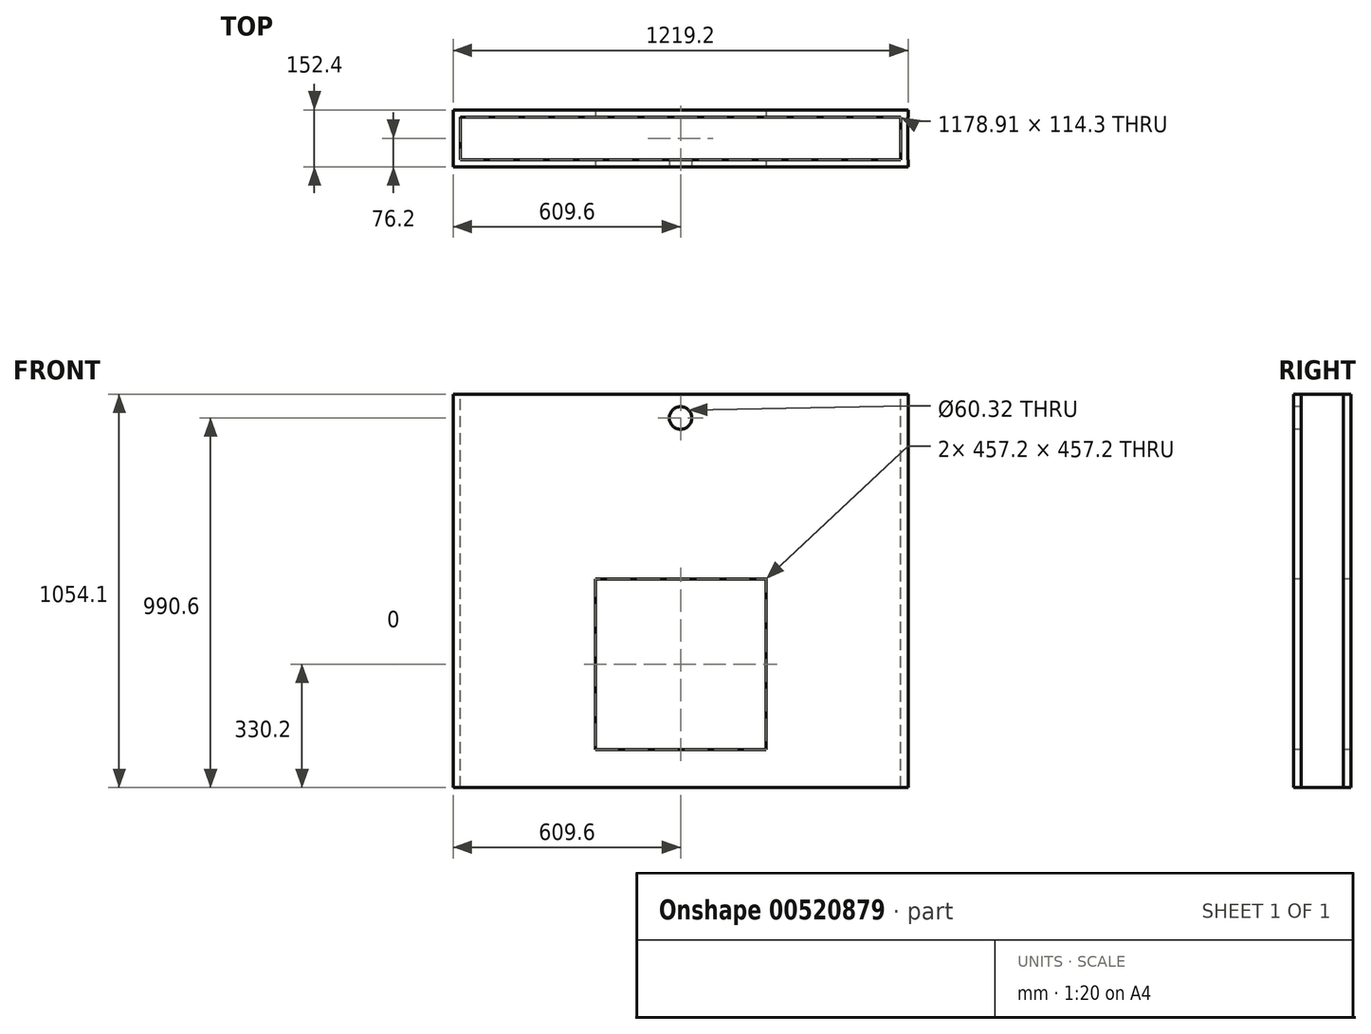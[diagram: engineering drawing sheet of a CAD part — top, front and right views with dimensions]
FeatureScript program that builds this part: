
annotation { "Feature Type Name" : "Feature", "Feature Type Description" : "" }
export const myFeature = defineFeature(function(context is Context, id is Id, definition is map)
    precondition{}
    {
        {
            var Q0;
            Q0=qCreatedBy(makeId("Top.planeOp"),FACE);
            var sketch = newSketch(context, id + "F0", { "sketchPlane" : qUnion([Q0])});
            skLineSegment(sketch, "E0.bottom", {"start": v(609.6, 76.2) * mm, "end": v(-609.6, 76.2) * mm});
            skLineSegment(sketch, "E0.top", {"start": v(609.6, -76.2) * mm, "end": v(-609.6, -76.2) * mm});
            skLineSegment(sketch, "E0.left", {"start": v(609.6, 76.2) * mm, "end": v(609.6, -76.2) * mm});
            skLineSegment(sketch, "E0.right", {"start": v(-609.6, 76.2) * mm, "end": v(-609.6, -76.2) * mm});
            skPoint(sketch, "E0.middle", {"position": v(0, 0) * mm});
            skLineSegment(sketch, "E1.bottom", {"start": v(-608.84, 57.15) * mm, "end": v(-610.36, 57.15) * mm});
            skLineSegment(sketch, "E1.top", {"start": v(-608.84, -57.15) * mm, "end": v(-610.36, -57.15) * mm});
            skLineSegment(sketch, "E1.left", {"start": v(-608.84, 57.15) * mm, "end": v(-608.84, -57.15) * mm});
            skLineSegment(sketch, "E1.right", {"start": v(-610.36, 57.15) * mm, "end": v(-610.36, -57.15) * mm});
            skPoint(sketch, "E1.middle", {"position": v(-609.6, 0) * mm});
            skLineSegment(sketch, "E2.bottom", {"start": v(610.36, 57.15) * mm, "end": v(608.84, 57.15) * mm});
            skLineSegment(sketch, "E2.top", {"start": v(610.36, -57.15) * mm, "end": v(608.84, -57.15) * mm});
            skLineSegment(sketch, "E2.left", {"start": v(610.36, 57.15) * mm, "end": v(610.36, -57.15) * mm});
            skLineSegment(sketch, "E2.right", {"start": v(608.84, 57.15) * mm, "end": v(608.84, -57.15) * mm});
            skPoint(sketch, "E2.middle", {"position": v(609.6, 0) * mm});
            skSolve(sketch);
        }
        {
            var Q0;
            {var subQ7=sQuery(id+"F0.wireOp",EDGE,"E0.bottom");Q0=makeQuery(id+"F0.imprint","IMPRINT",FACE,{"disambiguationData":[TD([[makeQuery(id+"F0.imprint","IMPRINT",EDGE,{"derivedFrom":subQ7}),1.0]])]});}
            extrude(context, id + "F1", {"entities" : qUnion([Q0]), "depth" : 1054.1 * mm, "offsetDistance" : 25.4 * mm});
        }
        {
            var Q0;
            Q0=makeQuery(id+"F1.opExtrude","SWEPT_FACE",FACE,{"disambiguationData":[OSD([sQuery(id+"F0.wireOp",EDGE,"E0.top")])]});
            var sketch = newSketch(context, id + "F2", { "sketchPlane" : qUnion([Q0])});
            skLineSegment(sketch, "E3", {"start": v(0, 0) * mm, "end": v(0, 101.6) * mm});
            skLineSegment(sketch, "E4", {"start": v(0, 101.6) * mm, "end": v(0, 330.2) * mm});
            skPoint(sketch, "E4.endSnap0", {"position": v(0, 50.8) * mm});
            skLineSegment(sketch, "E5.bottom", {"start": v(228.6, 101.6) * mm, "end": v(-228.6, 101.6) * mm});
            skLineSegment(sketch, "E5.top", {"start": v(228.6, 558.8) * mm, "end": v(-228.6, 558.8) * mm});
            skLineSegment(sketch, "E5.left", {"start": v(228.6, 101.6) * mm, "end": v(228.6, 558.8) * mm});
            skLineSegment(sketch, "E5.right", {"start": v(-228.6, 101.6) * mm, "end": v(-228.6, 558.8) * mm});
            skPoint(sketch, "E5.middle", {"position": v(0, 330.2) * mm});
            skSolve(sketch);
        }
        {
            var Q0;
            Q0=makeQuery(id+"F2.imprint","IMPRINT",FACE,{"disambiguationData":[TD([[makeQuery(id+"F2.imprint","IMPRINT",EDGE,{"derivedFrom":sQuery(id+"F2.wireOp",EDGE,"E5.top")}),1.0]])]});
            extrude(context, id + "F3", {"entities" : qUnion([Q0]), "operationType" : NewBodyOperationType.REMOVE, "oppositeDirection" : true, "depth" : 152.4 * mm, "offsetDistance" : 25.4 * mm});
        }
        {
            var Q0;
            Q0=makeQuery(id+"F1.opExtrude","CAP_FACE",FACE,{"disambiguationData":[OSD([sQuery(id+"F0.wireOp",EDGE,"E0.bottom"),sQuery(id+"F0.wireOp",EDGE,"E0.top"),sQuery(id+"F0.wireOp",EDGE,"E0.left"),sQuery(id+"F0.wireOp",EDGE,"E0.right"),sQuery(id+"F0.wireOp",EDGE,"E1.bottom"),sQuery(id+"F0.wireOp",EDGE,"E1.top"),sQuery(id+"F0.wireOp",EDGE,"E1.left"),sQuery(id+"F0.wireOp",EDGE,"E2.bottom"),sQuery(id+"F0.wireOp",EDGE,"E2.top"),sQuery(id+"F0.wireOp",EDGE,"E2.right")])],"isStart":false});
            var sketch = newSketch(context, id + "F4", { "sketchPlane" : qUnion([Q0])});
            skLineSegment(sketch, "E6.bottom", {"start": v(589.45, 57.15) * mm, "end": v(-589.45, 57.15) * mm});
            skLineSegment(sketch, "E6.top", {"start": v(589.45, -57.15) * mm, "end": v(-589.45, -57.15) * mm});
            skLineSegment(sketch, "E6.left", {"start": v(589.45, 57.15) * mm, "end": v(589.45, -57.15) * mm});
            skLineSegment(sketch, "E6.right", {"start": v(-589.45, 57.15) * mm, "end": v(-589.45, -57.15) * mm});
            skPoint(sketch, "E6.middle", {"position": v(0, 0) * mm});
            skSolve(sketch);
        }
        {
            var Q0;
            Q0=makeQuery(id+"F4.imprint","IMPRINT",FACE,{"disambiguationData":[TD([[makeQuery(id+"F4.imprint","IMPRINT",EDGE,{"derivedFrom":sQuery(id+"F4.wireOp",EDGE,"E6.bottom")}),1.0]])]});
            extrude(context, id + "F5", {"entities" : qUnion([Q0]), "operationType" : NewBodyOperationType.REMOVE, "oppositeDirection" : true, "depth" : 1270 * mm, "offsetDistance" : 25.4 * mm});
        }
        {
            var Q0;
            Q0=makeQuery(id+"F1.opExtrude","SWEPT_FACE",FACE,{"disambiguationData":[OSD([sQuery(id+"F0.wireOp",EDGE,"E0.top")])]});
            var sketch = newSketch(context, id + "F6", { "sketchPlane" : qUnion([Q0])});
            skLineSegment(sketch, "E7", {"start": v(0, 1054.1) * mm, "end": v(0, 990.6) * mm});
            skCircle(sketch, "E8", {"center": v(0, 990.6) * mm, "radius": 30.16 * mm});
            skSolve(sketch);
        }
        {
            var Q0;
            Q0=makeQuery(id+"F6.imprint","IMPRINT",FACE,{"disambiguationData":[TD([[makeQuery(id+"F6.imprint","IMPRINT",EDGE,{"derivedFrom":sQuery(id+"F6.wireOp",EDGE,"E8")}),1.0]])]});
            extrude(context, id + "F7", {"entities" : qUnion([Q0]), "operationType" : NewBodyOperationType.REMOVE, "oppositeDirection" : true, "depth" : 25.4 * mm, "offsetDistance" : 25.4 * mm});
        }
    });
